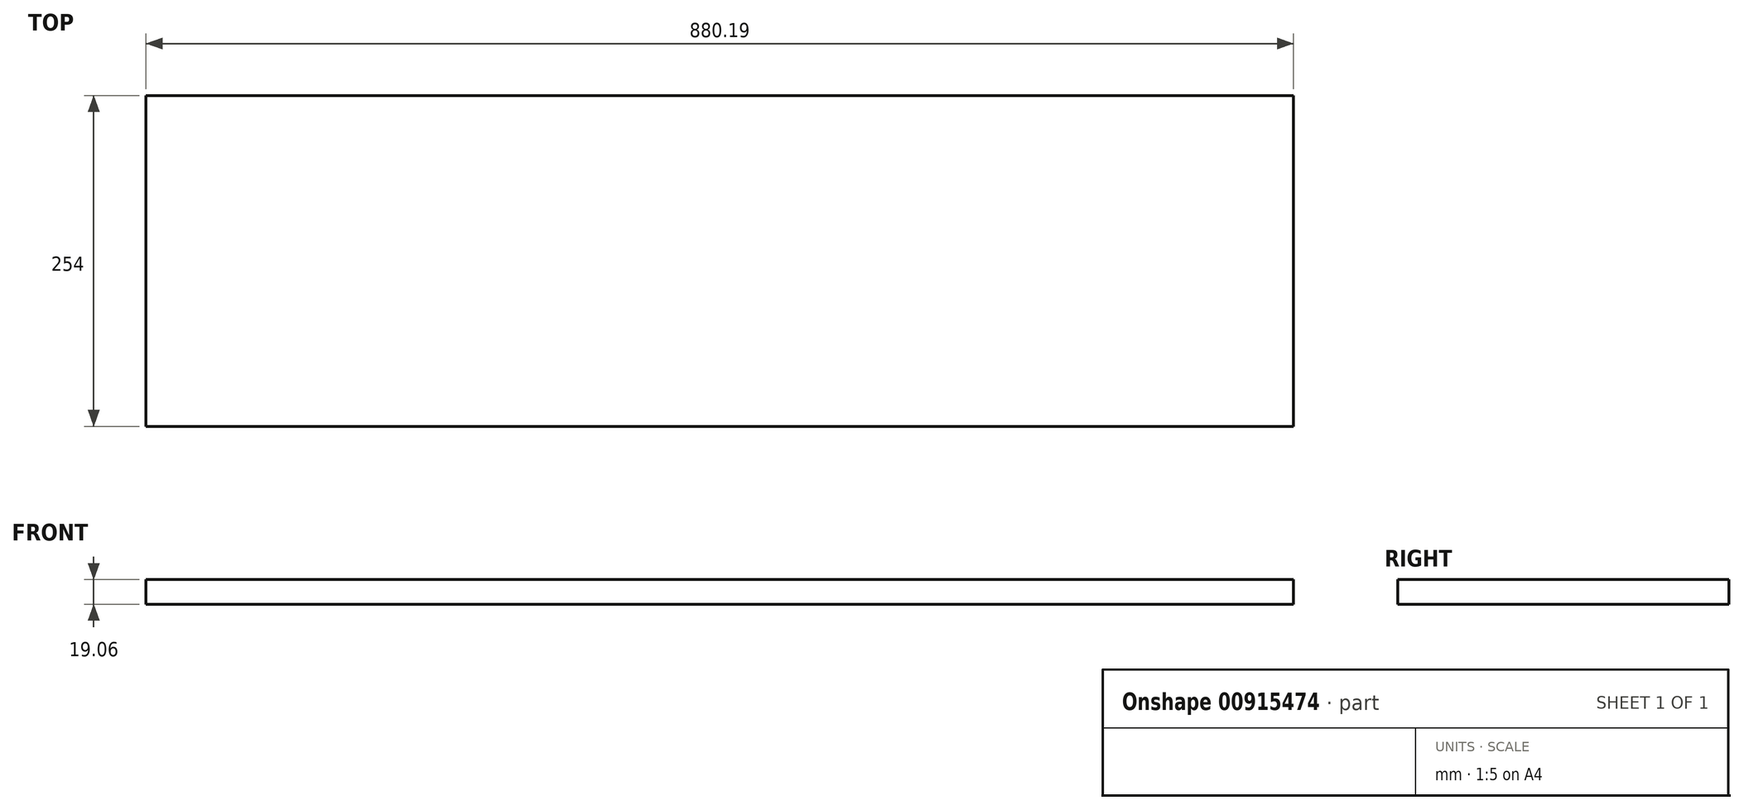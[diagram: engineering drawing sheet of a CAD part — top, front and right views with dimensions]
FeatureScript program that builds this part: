
annotation { "Feature Type Name" : "Feature", "Feature Type Description" : "" }
export const myFeature = defineFeature(function(context is Context, id is Id, definition is map)
    precondition{}
    {
        {
            var Q0;
            Q0=qCreatedBy(makeId("Right.planeOp"),FACE);
            var sketch = newSketch(context, id + "F0", { "sketchPlane" : qUnion([Q0])});
            skLineSegment(sketch, "E0.bottom", {"start": v(129.12, 9.52) * mm, "end": v(-124.88, 9.52) * mm});
            skLineSegment(sketch, "E0.top", {"start": v(129.12, -9.53) * mm, "end": v(-124.88, -9.53) * mm});
            skLineSegment(sketch, "E0.left", {"start": v(129.12, 9.52) * mm, "end": v(129.12, -9.53) * mm});
            skLineSegment(sketch, "E0.right", {"start": v(-124.88, 9.52) * mm, "end": v(-124.88, -9.53) * mm});
            skPoint(sketch, "E0.middle", {"position": v(2.12, 0) * mm});
            skSolve(sketch);
        }
        {
            var Q0;
            Q0=makeQuery(id+"F0.imprint","IMPRINT",FACE,{"disambiguationData":[TD([[makeQuery(id+"F0.imprint","IMPRINT",EDGE,{"derivedFrom":sQuery(id+"F0.wireOp",EDGE,"E0.bottom")}),1.0]])]});
            extrude(context, id + "F1", {"entities" : qUnion([Q0]), "depth" : 880.2 * mm, "offsetDistance" : 25.4 * mm});
        }
    });
